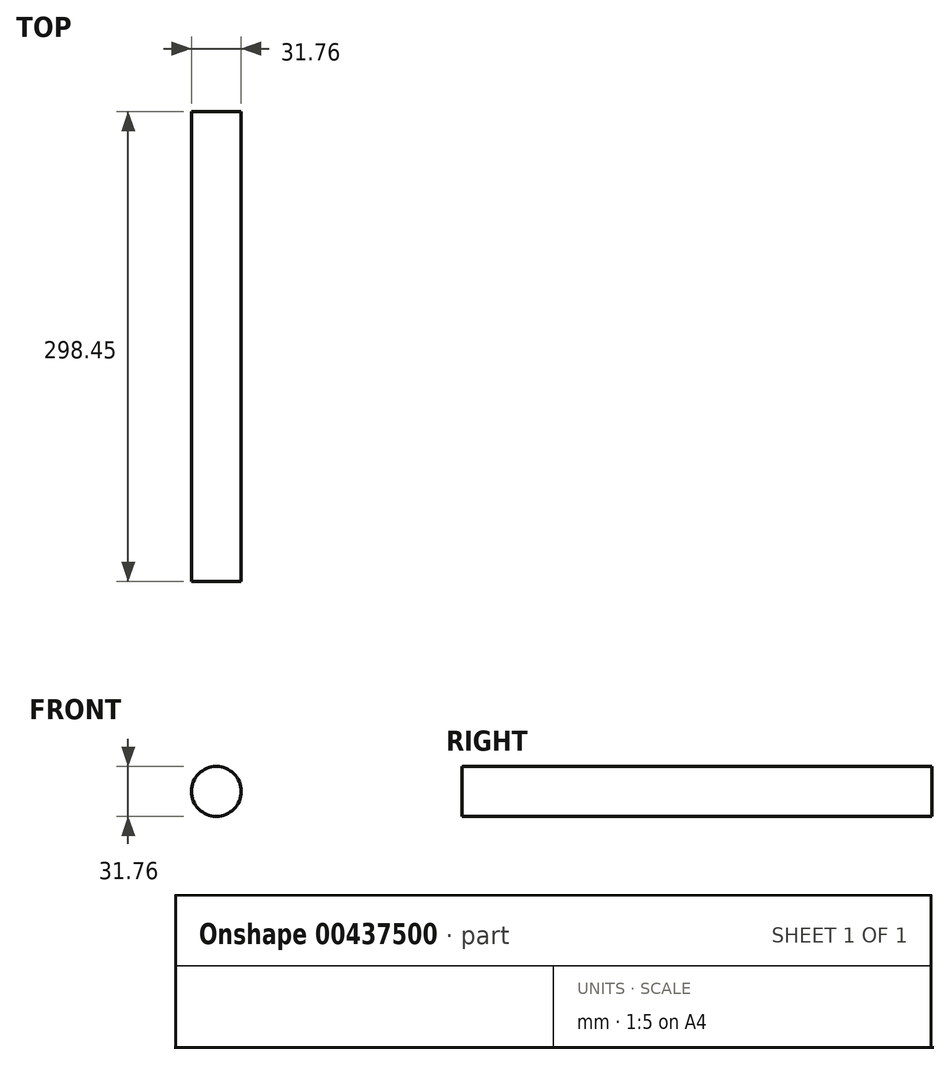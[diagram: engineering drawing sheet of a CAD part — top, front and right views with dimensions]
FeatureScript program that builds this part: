
annotation { "Feature Type Name" : "Feature", "Feature Type Description" : "" }
export const myFeature = defineFeature(function(context is Context, id is Id, definition is map)
    precondition{}
    {
        {
            var Q0;
            Q0=qCreatedBy(makeId("Front.planeOp"),FACE);
            var sketch = newSketch(context, id + "F0", { "sketchPlane" : qUnion([Q0])});
            skCircle(sketch, "E0", {"center": v(0, 0) * mm, "radius": 15.88 * mm});
            skSolve(sketch);
        }
        {
            var Q0;
            Q0 = qSketchRegion(id + "F0", true);
            extrude(context, id + "F1", {"entities" : qUnion([Q0]), "depth" : 298.45 * mm, "offsetDistance" : 25.4 * mm});
        }
    });
